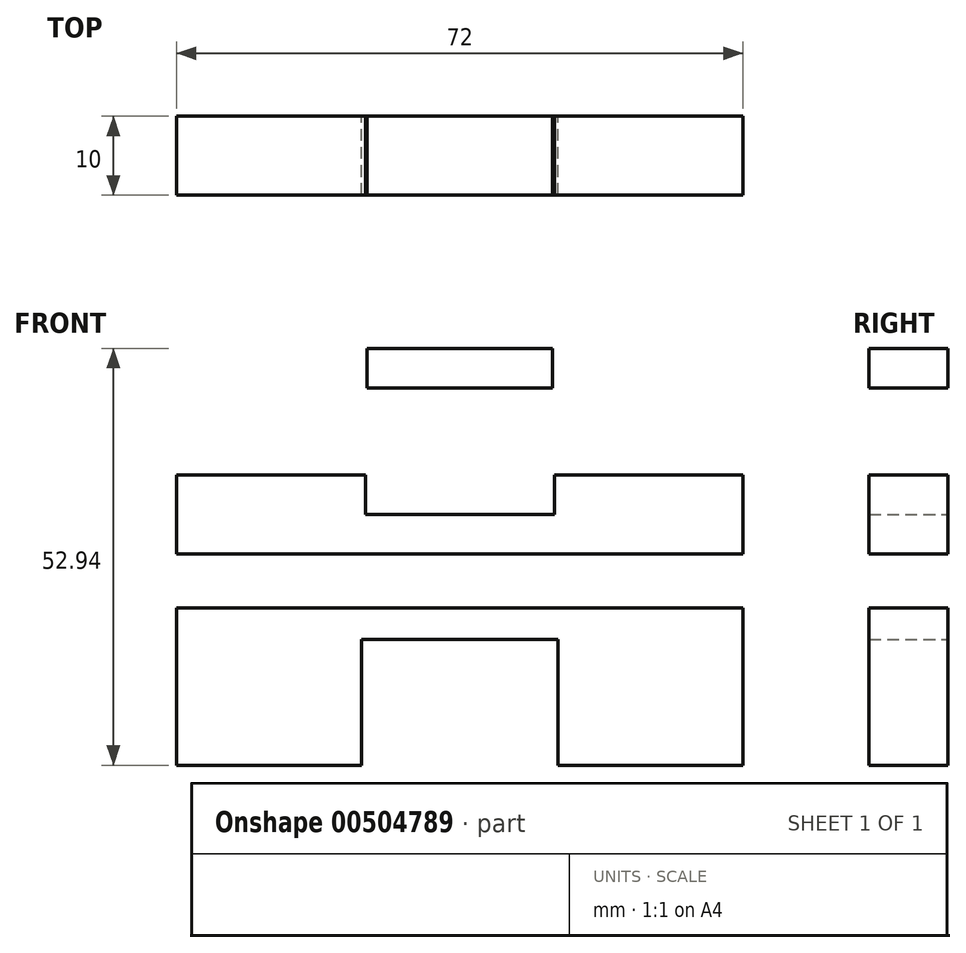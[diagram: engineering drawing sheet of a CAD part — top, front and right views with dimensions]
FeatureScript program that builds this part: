
annotation { "Feature Type Name" : "Feature", "Feature Type Description" : "" }
export const myFeature = defineFeature(function(context is Context, id is Id, definition is map)
    precondition{}
    {
        {
            var Q0;
            Q0=qCreatedBy(makeId("Front.planeOp"),FACE);
            var sketch = newSketch(context, id + "F0", { "sketchPlane" : qUnion([Q0])});
            skLineSegment(sketch, "E0.bottom", {"start": v(36, 5) * mm, "end": v(12, 5) * mm});
            skLineSegment(sketch, "E0.top", {"start": v(36, -5) * mm, "end": v(-36, -5) * mm});
            skLineSegment(sketch, "E0.left", {"start": v(36, 5) * mm, "end": v(36, -5) * mm});
            skLineSegment(sketch, "E0.right", {"start": v(-36, 5) * mm, "end": v(-36, -5) * mm});
            skPoint(sketch, "E0.middle", {"position": v(0, 0) * mm});
            skLineSegment(sketch, "E1.top", {"start": v(-12, 0) * mm, "end": v(12, 0) * mm});
            skLineSegment(sketch, "E1.left", {"start": v(-12, 5) * mm, "end": v(-12, 0) * mm});
            skLineSegment(sketch, "E1.right", {"start": v(12, 5) * mm, "end": v(12, 0) * mm});
            skLineSegment(sketch, "E2.trimOffspring", {"start": v(-12, 5) * mm, "end": v(-36, 5) * mm});
            skSolve(sketch);
        }
        {
            var Q0;
            Q0=makeQuery(id+"F0.imprint","IMPRINT",FACE,{"disambiguationData":[TD([[makeQuery(id+"F0.imprint","IMPRINT",EDGE,{"derivedFrom":sQuery(id+"F0.wireOp",EDGE,"E0.bottom")}),1.0]])]});
            extrude(context, id + "F1", {"entities" : qUnion([Q0]), "endBound" : BoundingType.SYMMETRIC, "depth" : 10 * mm});
        }
        {
            var Q0;
            Q0=qCreatedBy(makeId("Front.planeOp"),FACE);
            var sketch = newSketch(context, id + "F2", { "sketchPlane" : qUnion([Q0])});
            skLineSegment(sketch, "E3.bottom", {"start": v(11.75, 21.07) * mm, "end": v(-11.75, 21.07) * mm});
            skLineSegment(sketch, "E3.top", {"start": v(11.75, 16.07) * mm, "end": v(-11.75, 16.07) * mm});
            skLineSegment(sketch, "E3.left", {"start": v(11.75, 21.07) * mm, "end": v(11.75, 16.07) * mm});
            skLineSegment(sketch, "E3.right", {"start": v(-11.75, 21.07) * mm, "end": v(-11.75, 16.07) * mm});
            skPoint(sketch, "E3.middle", {"position": v(0, 18.57) * mm});
            skSolve(sketch);
        }
        {
            var Q0;
            Q0=makeQuery(id+"F2.imprint","IMPRINT",FACE,{"disambiguationData":[TD([[makeQuery(id+"F2.imprint","IMPRINT",EDGE,{"derivedFrom":sQuery(id+"F2.wireOp",EDGE,"E3.bottom")}),1.0]])]});
            extrude(context, id + "F3", {"entities" : qUnion([Q0]), "endBound" : BoundingType.SYMMETRIC, "depth" : 10 * mm});
        }
        {
            var Q0;
            Q0=qCreatedBy(makeId("Front.planeOp"),FACE);
            var sketch = newSketch(context, id + "F4", { "sketchPlane" : qUnion([Q0])});
            skLineSegment(sketch, "E4.bottom", {"start": v(36, -31.87) * mm, "end": v(12.5, -31.87) * mm});
            skLineSegment(sketch, "E4.top", {"start": v(36, -11.87) * mm, "end": v(-36, -11.87) * mm});
            skLineSegment(sketch, "E4.left", {"start": v(36, -31.87) * mm, "end": v(36, -11.87) * mm});
            skLineSegment(sketch, "E4.right", {"start": v(-36, -31.87) * mm, "end": v(-36, -11.87) * mm});
            skPoint(sketch, "E4.middle", {"position": v(0, -21.87) * mm});
            skLineSegment(sketch, "E5.top", {"start": v(-12.5, -15.87) * mm, "end": v(12.5, -15.87) * mm});
            skLineSegment(sketch, "E5.left", {"start": v(-12.5, -31.87) * mm, "end": v(-12.5, -15.87) * mm});
            skLineSegment(sketch, "E5.right", {"start": v(12.5, -31.87) * mm, "end": v(12.5, -15.87) * mm});
            skLineSegment(sketch, "E6.trimOffspring", {"start": v(-12.5, -31.87) * mm, "end": v(-36, -31.87) * mm});
            skSolve(sketch);
        }
        {
            var Q0;
            Q0=makeQuery(id+"F4.imprint","IMPRINT",FACE,{"disambiguationData":[TD([[makeQuery(id+"F4.imprint","IMPRINT",EDGE,{"derivedFrom":sQuery(id+"F4.wireOp",EDGE,"E4.bottom")}),-1.0]])]});
            extrude(context, id + "F5", {"entities" : qUnion([Q0]), "endBound" : BoundingType.SYMMETRIC, "depth" : 10 * mm});
        }
    });
